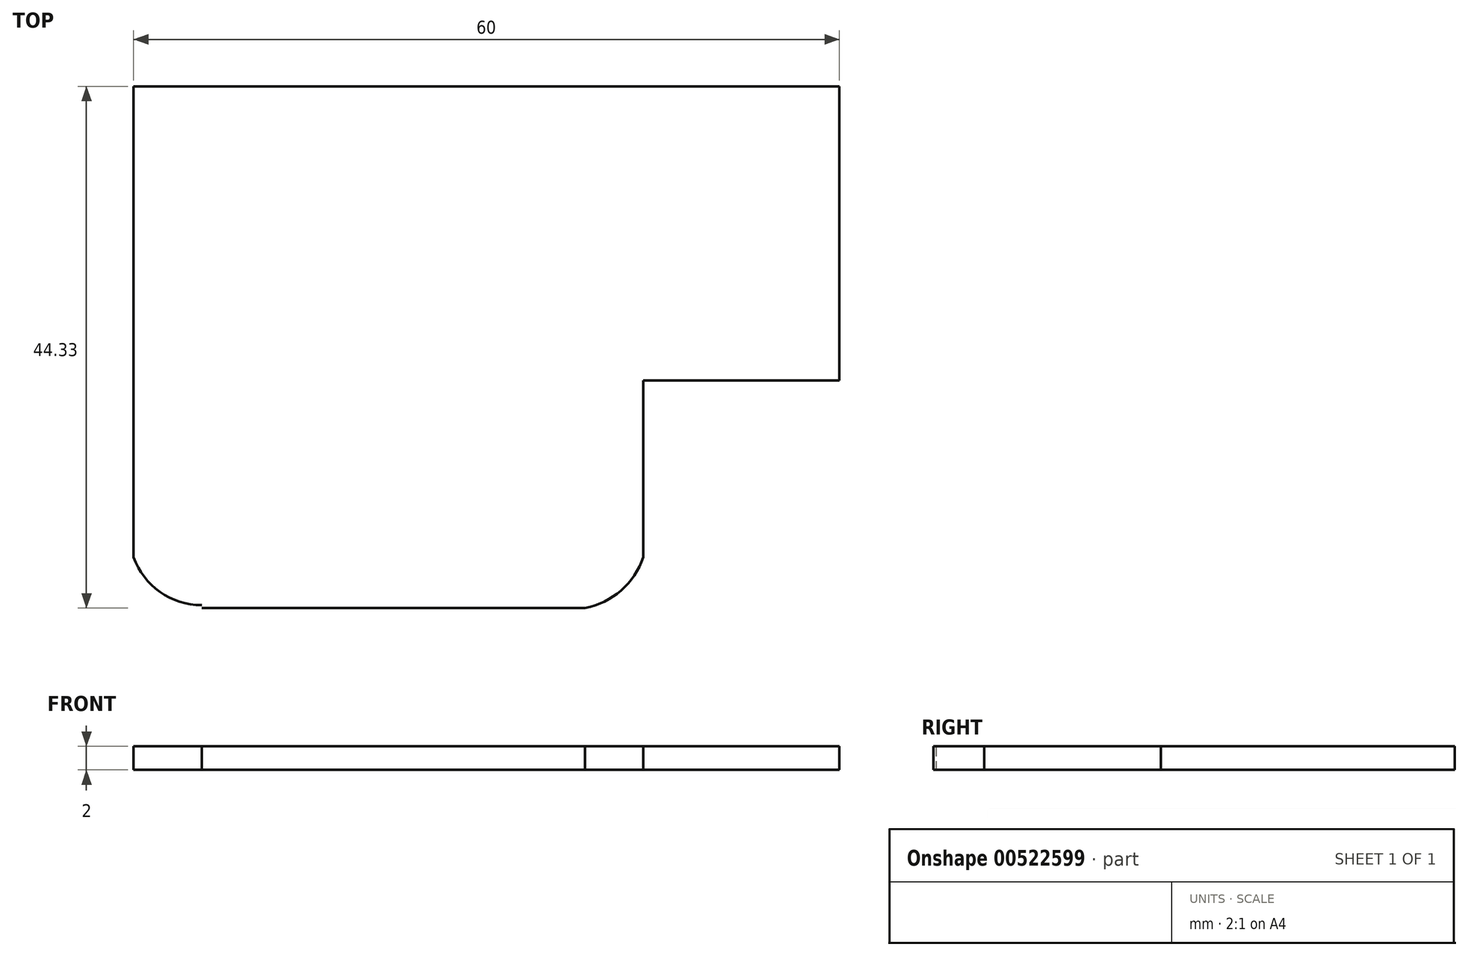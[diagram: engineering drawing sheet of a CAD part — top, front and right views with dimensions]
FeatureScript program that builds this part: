
annotation { "Feature Type Name" : "Feature", "Feature Type Description" : "" }
export const myFeature = defineFeature(function(context is Context, id is Id, definition is map)
    precondition{}
    {
        {
            var Q0;
            Q0=qCreatedBy(makeId("Top.planeOp"),FACE);
            var sketch = newSketch(context, id + "F0", { "sketchPlane" : qUnion([Q0])});
            skLineSegment(sketch, "E0", {"start": v(0, 0) * mm, "end": v(60, 0) * mm});
            skLineSegment(sketch, "E1", {"start": v(60, 0) * mm, "end": v(60, -25) * mm});
            skLineSegment(sketch, "E2", {"start": v(60, -25) * mm, "end": v(43.33, -25) * mm});
            skLineSegment(sketch, "E3", {"start": v(0, 0) * mm, "end": v(0, -40) * mm});
            skLineSegment(sketch, "E4", {"start": v(43.33, -25) * mm, "end": v(43.33, -40) * mm});
            skArc(sketch, "E5", {"start": v(38.39, -44.33) * mm, "mid": v(41.44, -42.83) * mm, "end": v(43.33, -40) * mm});
            skLineSegment(sketch, "E6", {"start": v(38.39, -44.33) * mm, "end": v(5.79, -44.33) * mm});
            skArc(sketch, "E7", {"start": v(0, -40) * mm, "mid": v(2.25, -42.96) * mm, "end": v(5.79, -44.08) * mm});
            skSolve(sketch);
        }
        {
            var Q0;
            Q0=sQuery(id+"F0.wireOp",EDGE,"E5");
            var Q1;
            Q1=sQuery(id+"F0.wireOp",EDGE,"E4");
            var Q2;
            Q2=sQuery(id+"F0.wireOp",EDGE,"E0");
            var Q3;
            Q3=sQuery(id+"F0.wireOp",EDGE,"E2");
            var Q4;
            Q4=sQuery(id+"F0.wireOp",EDGE,"E6");
            var Q5;
            Q5=sQuery(id+"F0.wireOp",EDGE,"E3");
            var Q6;
            Q6=sQuery(id+"F0.wireOp",EDGE,"E1");
            var Q7;
            Q7=sQuery(id+"F0.wireOp",EDGE,"E7");
            extrude(context, id + "F1", {"bodyType" : ToolBodyType.SURFACE, "surfaceEntities" : qUnion([Q0, Q1, Q2, Q3, Q4, Q5, Q6, Q7]), "depth" : 2 * mm, "offsetDistance" : 25 * mm});
        }
    });
